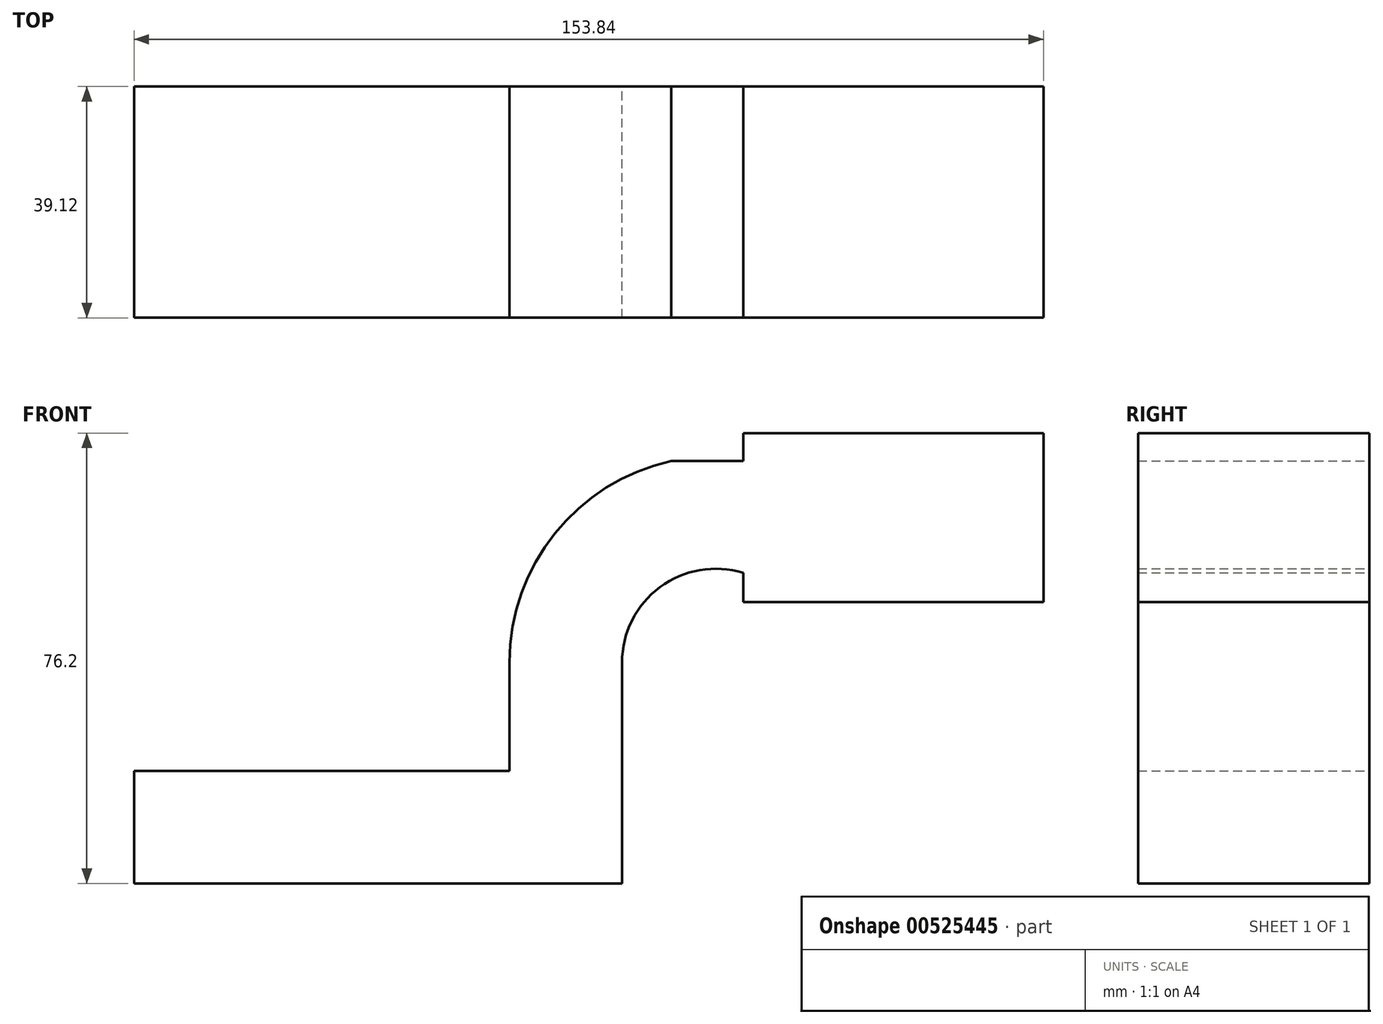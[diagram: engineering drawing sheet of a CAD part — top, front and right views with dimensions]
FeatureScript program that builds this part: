
annotation { "Feature Type Name" : "Feature", "Feature Type Description" : "" }
export const myFeature = defineFeature(function(context is Context, id is Id, definition is map)
    precondition{}
    {
        {
            var Q0;
            Q0=qCreatedBy(makeId("Front.planeOp"),FACE);
            var sketch = newSketch(context, id + "F0", { "sketchPlane" : qUnion([Q0])});
            skLineSegment(sketch, "E0.bottom", {"start": v(-41.28, 9.52) * mm, "end": v(41.27, 9.53) * mm});
            skLineSegment(sketch, "E0.top", {"start": v(-41.28, -9.53) * mm, "end": v(41.28, -9.53) * mm});
            skLineSegment(sketch, "E0.left", {"start": v(-41.28, 9.52) * mm, "end": v(-41.28, -9.53) * mm});
            skLineSegment(sketch, "E0.right", {"start": v(41.27, 9.53) * mm, "end": v(41.28, -9.52) * mm});
            skPoint(sketch, "E0.middle", {"position": v(0, 0) * mm});
            skLineSegment(sketch, "E1.bottom", {"start": v(61.77, 38.1) * mm, "end": v(112.57, 38.1) * mm});
            skLineSegment(sketch, "E1.top", {"start": v(61.77, 66.67) * mm, "end": v(112.57, 66.67) * mm});
            skLineSegment(sketch, "E1.left", {"start": v(61.77, 38.1) * mm, "end": v(61.77, 66.67) * mm});
            skLineSegment(sketch, "E1.right", {"start": v(112.57, 38.1) * mm, "end": v(112.57, 66.67) * mm});
            skPoint(sketch, "E1.middle", {"position": v(87.17, 52.39) * mm});
            skLineSegment(sketch, "E2", {"start": v(41.27, 9.53) * mm, "end": v(41.27, 27.83) * mm});
            skArc(sketch, "E3", {"start": v(41.27, 27.83) * mm, "mid": v(47.88, 40.72) * mm, "end": v(62.2, 42.88) * mm});
            skLineSegment(sketch, "E4", {"start": v(62.2, 42.88) * mm, "end": v(87.88, 42.88) * mm});
            skLineSegment(sketch, "E5.0", {"start": v(49.6, 61.93) * mm, "end": v(87.88, 61.93) * mm});
            skArc(sketch, "E5.1", {"start": v(22.23, 27.83) * mm, "mid": v(29.91, 49.69) * mm, "end": v(49.6, 61.93) * mm});
            skLineSegment(sketch, "E5.2", {"start": v(22.22, 9.53) * mm, "end": v(22.22, 27.83) * mm});
            skFitSpline(sketch, "E6", {"points": [v(-41.28, 9.53) * mm, v(49.6, 61.93) * mm], "startDerivative": vector(47.1, 122.34) * mm, "endDerivative": vector(115.37, -1.13) * mm});
            skSolve(sketch);
        }
        {
            var Q0;
            Q0=makeQuery(id+"F0.imprint","IMPRINT",FACE,{"disambiguationData":[TD([[makeQuery(id+"F0.imprint","IMPRINT",EDGE,{"derivedFrom":sQuery(id+"F0.wireOp",EDGE,"E5.1")}),1.0]])]});
            var Q1;
            Q1=makeQuery(id+"F0.imprint","IMPRINT",FACE,{"disambiguationData":[TD([[makeQuery(id+"F0.imprint","IMPRINT",EDGE,{"derivedFrom":sQuery(id+"F0.wireOp",EDGE,"E0.top")}),1.0]])]});
            var Q2;
            {var subQ1=sQuery(id+"F0.wireOp",EDGE,"E2");Q2=makeQuery(id+"F0.imprint","IMPRINT",FACE,{"disambiguationData":[TD([[makeQuery(id+"F0.imprint","IMPRINT",EDGE,{"derivedFrom":subQ1}),1.0]])]});}
            var Q3;
            {var subQ3=sQuery(id+"F0.wireOp",EDGE,"E1.bottom");Q3=makeQuery(id+"F0.imprint","IMPRINT",FACE,{"disambiguationData":[TD([[makeQuery(id+"F0.imprint","IMPRINT",EDGE,{"derivedFrom":subQ3}),1.0]])]});}
            extrude(context, id + "F1", {"entities" : qUnion([Q0, Q1, Q2, Q3]), "depth" : 39.12 * mm, "offsetDistance" : 25.4 * mm});
        }
    });
